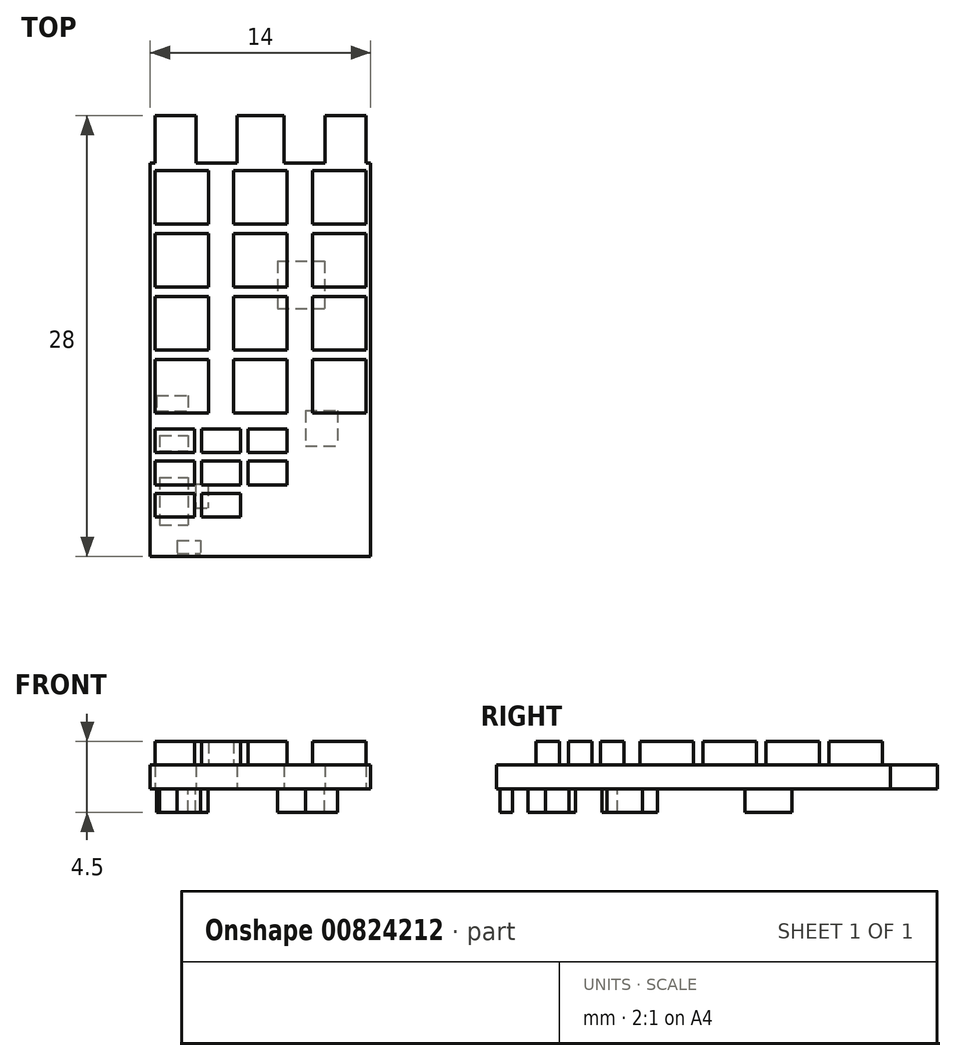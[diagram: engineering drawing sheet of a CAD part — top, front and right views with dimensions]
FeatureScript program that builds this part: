
annotation { "Feature Type Name" : "Feature", "Feature Type Description" : "" }
export const myFeature = defineFeature(function(context is Context, id is Id, definition is map)
    precondition{}
    {
        {
            var Q0;
            Q0=qCreatedBy(makeId("Top.planeOp"),FACE);
            var sketch = newSketch(context, id + "F0", { "sketchPlane" : qUnion([Q0])});
            skLineSegment(sketch, "E0.bottom", {"start": v(7, -14) * mm, "end": v(-7, -14) * mm});
            skLineSegment(sketch, "E0.top", {"start": v(7, 14) * mm, "end": v(-7, 14) * mm});
            skLineSegment(sketch, "E0.left", {"start": v(7, -14) * mm, "end": v(7, 14) * mm});
            skLineSegment(sketch, "E0.right", {"start": v(-7, -14) * mm, "end": v(-7, 14) * mm});
            skPoint(sketch, "E0.middle", {"position": v(0, 0) * mm});
            skLineSegment(sketch, "E1", {"start": v(-4.1, 14) * mm, "end": v(-4.1, 11) * mm});
            skLineSegment(sketch, "E2", {"start": v(-4.1, 11) * mm, "end": v(-1.5, 11) * mm});
            skLineSegment(sketch, "E3", {"start": v(-1.5, 11) * mm, "end": v(-1.5, 14) * mm});
            skLineSegment(sketch, "E4", {"start": v(-1.5, 14) * mm, "end": v(1.5, 14) * mm});
            skLineSegment(sketch, "E5", {"start": v(1.5, 14) * mm, "end": v(1.5, 11) * mm});
            skLineSegment(sketch, "E6", {"start": v(1.5, 11) * mm, "end": v(4.1, 11) * mm});
            skLineSegment(sketch, "E7", {"start": v(4.1, 11) * mm, "end": v(4.1, 14) * mm});
            skLineSegment(sketch, "E8", {"start": v(-6.7, 14) * mm, "end": v(-6.7, 11) * mm});
            skLineSegment(sketch, "E9", {"start": v(-6.7, 11) * mm, "end": v(-7, 11) * mm});
            skLineSegment(sketch, "E10", {"start": v(6.7, 14) * mm, "end": v(6.7, 11) * mm});
            skLineSegment(sketch, "E11", {"start": v(6.7, 11) * mm, "end": v(7, 11) * mm});
            skLineSegment(sketch, "E12", {"start": v(0, 14) * mm, "end": v(0, -14) * mm, "construction": true});
            skSolve(sketch);
        }
        {
            var Q0;
            {var subQ1=sQuery(id+"F0.wireOp",EDGE,"E0.bottom");Q0=makeQuery(id+"F0.imprint","IMPRINT",FACE,{"disambiguationData":[TD([[makeQuery(id+"F0.imprint","IMPRINT",EDGE,{"derivedFrom":subQ1}),-1.0]])]});}
            extrude(context, id + "F1", {"entities" : qUnion([Q0]), "depth" : 1.5 * mm, "offsetDistance" : 25 * mm});
        }
        {
            var Q0;
            Q0=makeQuery(id+"F1.opExtrude","CAP_FACE",FACE,{"disambiguationData":[OSD([sQuery(id+"F0.wireOp",EDGE,"E0.bottom"),sQuery(id+"F0.wireOp",EDGE,"E0.top"),sQuery(id+"F0.wireOp",EDGE,"E0.left"),sQuery(id+"F0.wireOp",EDGE,"E0.right"),sQuery(id+"F0.wireOp",EDGE,"E1"),sQuery(id+"F0.wireOp",EDGE,"E2"),sQuery(id+"F0.wireOp",EDGE,"E3"),sQuery(id+"F0.wireOp",EDGE,"E4"),sQuery(id+"F0.wireOp",EDGE,"E5"),sQuery(id+"F0.wireOp",EDGE,"E6"),sQuery(id+"F0.wireOp",EDGE,"E7"),sQuery(id+"F0.wireOp",EDGE,"E8"),sQuery(id+"F0.wireOp",EDGE,"E9"),sQuery(id+"F0.wireOp",EDGE,"E10"),sQuery(id+"F0.wireOp",EDGE,"E11")])],"isStart":false});
            var sketch = newSketch(context, id + "F2", { "sketchPlane" : qUnion([Q0])});
            skSolve(sketch);
        }
        {
            var Q0;
            Q0=makeQuery(id+"F2.imprint","IMPRINT",FACE,{"disambiguationData":[TD([[makeQuery(id+"F2.imprint","IMPRINT",EDGE,{"derivedFrom":makeQuery(id+"F1.opExtrude","CAP_EDGE",EDGE,{"disambiguationData":[OSD([sQuery(id+"F0.wireOp",EDGE,"E0.bottom")])],"isStart":false})}),-1.0]])]});
            var sketch = newSketch(context, id + "F3", { "sketchPlane" : qUnion([Q0])});
            skLineSegment(sketch, "E13.bottom", {"start": v(-3.3, 10.5) * mm, "end": v(-6.7, 10.5) * mm});
            skLineSegment(sketch, "E13.top", {"start": v(-3.3, 7.1) * mm, "end": v(-6.7, 7.1) * mm});
            skLineSegment(sketch, "E13.left", {"start": v(-3.3, 10.5) * mm, "end": v(-3.3, 7.1) * mm});
            skLineSegment(sketch, "E13.right", {"start": v(-6.7, 10.5) * mm, "end": v(-6.7, 7.1) * mm});
            skPoint(sketch, "E13.middle", {"position": v(-5, 8.8) * mm});
            skLineSegment(sketch, "E14.0.1.0", {"start": v(-6.7, 6.5) * mm, "end": v(-6.7, 3.1) * mm});
            skLineSegment(sketch, "E14.0.1.1", {"start": v(-3.3, 6.5) * mm, "end": v(-6.7, 6.5) * mm});
            skLineSegment(sketch, "E14.0.1.2", {"start": v(-3.3, 6.5) * mm, "end": v(-3.3, 3.1) * mm});
            skLineSegment(sketch, "E14.0.1.3", {"start": v(-3.3, 3.1) * mm, "end": v(-6.7, 3.1) * mm});
            skPoint(sketch, "E14.0.1.4", {"position": v(-5, 4.8) * mm});
            skLineSegment(sketch, "E14.0.2.0", {"start": v(-6.7, 2.5) * mm, "end": v(-6.7, -0.9) * mm});
            skLineSegment(sketch, "E14.0.2.1", {"start": v(-3.3, 2.5) * mm, "end": v(-6.7, 2.5) * mm});
            skLineSegment(sketch, "E14.0.2.2", {"start": v(-3.3, 2.5) * mm, "end": v(-3.3, -0.9) * mm});
            skLineSegment(sketch, "E14.0.2.3", {"start": v(-3.3, -0.9) * mm, "end": v(-6.7, -0.9) * mm});
            skPoint(sketch, "E14.0.2.4", {"position": v(-5, 0.8) * mm});
            skLineSegment(sketch, "E14.0.3.0", {"start": v(-6.7, -1.5) * mm, "end": v(-6.7, -4.9) * mm});
            skLineSegment(sketch, "E14.0.3.1", {"start": v(-3.3, -1.5) * mm, "end": v(-6.7, -1.5) * mm});
            skLineSegment(sketch, "E14.0.3.2", {"start": v(-3.3, -1.5) * mm, "end": v(-3.3, -4.9) * mm});
            skLineSegment(sketch, "E14.0.3.3", {"start": v(-3.3, -4.9) * mm, "end": v(-6.7, -4.9) * mm});
            skPoint(sketch, "E14.0.3.4", {"position": v(-5, -3.2) * mm});
            skLineSegment(sketch, "E14.1.0.0", {"start": v(-1.7, 10.5) * mm, "end": v(-1.7, 7.1) * mm});
            skLineSegment(sketch, "E14.1.0.1", {"start": v(1.7, 10.5) * mm, "end": v(-1.7, 10.5) * mm});
            skLineSegment(sketch, "E14.1.0.2", {"start": v(1.7, 10.5) * mm, "end": v(1.7, 7.1) * mm});
            skLineSegment(sketch, "E14.1.0.3", {"start": v(1.7, 7.1) * mm, "end": v(-1.7, 7.1) * mm});
            skPoint(sketch, "E14.1.0.4", {"position": v(0, 8.8) * mm});
            skLineSegment(sketch, "E14.1.1.0", {"start": v(-1.7, 6.5) * mm, "end": v(-1.7, 3.1) * mm});
            skLineSegment(sketch, "E14.1.1.1", {"start": v(1.7, 6.5) * mm, "end": v(-1.7, 6.5) * mm});
            skLineSegment(sketch, "E14.1.1.2", {"start": v(1.7, 6.5) * mm, "end": v(1.7, 3.1) * mm});
            skLineSegment(sketch, "E14.1.1.3", {"start": v(1.7, 3.1) * mm, "end": v(-1.7, 3.1) * mm});
            skPoint(sketch, "E14.1.1.4", {"position": v(0, 4.8) * mm});
            skLineSegment(sketch, "E14.1.2.0", {"start": v(-1.7, 2.5) * mm, "end": v(-1.7, -0.9) * mm});
            skLineSegment(sketch, "E14.1.2.1", {"start": v(1.7, 2.5) * mm, "end": v(-1.7, 2.5) * mm});
            skLineSegment(sketch, "E14.1.2.2", {"start": v(1.7, 2.5) * mm, "end": v(1.7, -0.9) * mm});
            skLineSegment(sketch, "E14.1.2.3", {"start": v(1.7, -0.9) * mm, "end": v(-1.7, -0.9) * mm});
            skPoint(sketch, "E14.1.2.4", {"position": v(0, 0.8) * mm});
            skLineSegment(sketch, "E14.1.3.0", {"start": v(-1.7, -1.5) * mm, "end": v(-1.7, -4.9) * mm});
            skLineSegment(sketch, "E14.1.3.1", {"start": v(1.7, -1.5) * mm, "end": v(-1.7, -1.5) * mm});
            skLineSegment(sketch, "E14.1.3.2", {"start": v(1.7, -1.5) * mm, "end": v(1.7, -4.9) * mm});
            skLineSegment(sketch, "E14.1.3.3", {"start": v(1.7, -4.9) * mm, "end": v(-1.7, -4.9) * mm});
            skPoint(sketch, "E14.1.3.4", {"position": v(0, -3.2) * mm});
            skLineSegment(sketch, "E14.2.0.0", {"start": v(3.3, 10.5) * mm, "end": v(3.3, 7.1) * mm});
            skLineSegment(sketch, "E14.2.0.1", {"start": v(6.7, 10.5) * mm, "end": v(3.3, 10.5) * mm});
            skLineSegment(sketch, "E14.2.0.2", {"start": v(6.7, 10.5) * mm, "end": v(6.7, 7.1) * mm});
            skLineSegment(sketch, "E14.2.0.3", {"start": v(6.7, 7.1) * mm, "end": v(3.3, 7.1) * mm});
            skPoint(sketch, "E14.2.0.4", {"position": v(5, 8.8) * mm});
            skLineSegment(sketch, "E14.2.1.0", {"start": v(3.3, 6.5) * mm, "end": v(3.3, 3.1) * mm});
            skLineSegment(sketch, "E14.2.1.1", {"start": v(6.7, 6.5) * mm, "end": v(3.3, 6.5) * mm});
            skLineSegment(sketch, "E14.2.1.2", {"start": v(6.7, 6.5) * mm, "end": v(6.7, 3.1) * mm});
            skLineSegment(sketch, "E14.2.1.3", {"start": v(6.7, 3.1) * mm, "end": v(3.3, 3.1) * mm});
            skPoint(sketch, "E14.2.1.4", {"position": v(5, 4.8) * mm});
            skLineSegment(sketch, "E14.2.2.0", {"start": v(3.3, 2.5) * mm, "end": v(3.3, -0.9) * mm});
            skLineSegment(sketch, "E14.2.2.1", {"start": v(6.7, 2.5) * mm, "end": v(3.3, 2.5) * mm});
            skLineSegment(sketch, "E14.2.2.2", {"start": v(6.7, 2.5) * mm, "end": v(6.7, -0.9) * mm});
            skLineSegment(sketch, "E14.2.2.3", {"start": v(6.7, -0.9) * mm, "end": v(3.3, -0.9) * mm});
            skPoint(sketch, "E14.2.2.4", {"position": v(5, 0.8) * mm});
            skLineSegment(sketch, "E14.2.3.0", {"start": v(3.3, -1.5) * mm, "end": v(3.3, -4.9) * mm});
            skLineSegment(sketch, "E14.2.3.1", {"start": v(6.7, -1.5) * mm, "end": v(3.3, -1.5) * mm});
            skLineSegment(sketch, "E14.2.3.2", {"start": v(6.7, -1.5) * mm, "end": v(6.7, -4.9) * mm});
            skLineSegment(sketch, "E14.2.3.3", {"start": v(6.7, -4.9) * mm, "end": v(3.3, -4.9) * mm});
            skPoint(sketch, "E14.2.3.4", {"position": v(5, -3.2) * mm});
            skLineSegment(sketch, "E14.direction1", {"start": v(-6.7, 7.1) * mm, "end": v(-1.7, 7.1) * mm, "construction": true});
            skLineSegment(sketch, "E14.direction2", {"start": v(-6.7, 7.1) * mm, "end": v(-6.7, 3.1) * mm, "construction": true});
            skLineSegment(sketch, "E15.bottom", {"start": v(-4.2, -7.4) * mm, "end": v(-6.7, -7.4) * mm});
            skLineSegment(sketch, "E15.top", {"start": v(-4.2, -5.9) * mm, "end": v(-6.7, -5.9) * mm});
            skLineSegment(sketch, "E15.left", {"start": v(-4.2, -7.4) * mm, "end": v(-4.2, -5.9) * mm});
            skLineSegment(sketch, "E15.right", {"start": v(-6.7, -7.4) * mm, "end": v(-6.7, -5.9) * mm});
            skPoint(sketch, "E15.middle", {"position": v(-5.45, -6.65) * mm});
            skLineSegment(sketch, "E16.0.1.0", {"start": v(-6.7, -9.45) * mm, "end": v(-6.7, -7.95) * mm});
            skLineSegment(sketch, "E16.0.1.1", {"start": v(-4.2, -7.95) * mm, "end": v(-6.7, -7.95) * mm});
            skLineSegment(sketch, "E16.0.1.2", {"start": v(-4.2, -9.45) * mm, "end": v(-6.7, -9.45) * mm});
            skPoint(sketch, "E16.0.1.3", {"position": v(-5.45, -8.7) * mm});
            skLineSegment(sketch, "E16.0.1.4", {"start": v(-4.2, -9.45) * mm, "end": v(-4.2, -7.95) * mm});
            skLineSegment(sketch, "E16.1.0.0", {"start": v(-3.75, -7.4) * mm, "end": v(-3.75, -5.9) * mm});
            skLineSegment(sketch, "E16.1.0.1", {"start": v(-1.25, -5.9) * mm, "end": v(-3.75, -5.9) * mm});
            skLineSegment(sketch, "E16.1.0.2", {"start": v(-1.25, -7.4) * mm, "end": v(-3.75, -7.4) * mm});
            skPoint(sketch, "E16.1.0.3", {"position": v(-2.5, -6.65) * mm});
            skLineSegment(sketch, "E16.1.0.4", {"start": v(-1.25, -7.4) * mm, "end": v(-1.25, -5.9) * mm});
            skLineSegment(sketch, "E16.1.1.0", {"start": v(-3.75, -9.45) * mm, "end": v(-3.75, -7.95) * mm});
            skLineSegment(sketch, "E16.1.1.1", {"start": v(-1.25, -7.95) * mm, "end": v(-3.75, -7.95) * mm});
            skLineSegment(sketch, "E16.1.1.2", {"start": v(-1.25, -9.45) * mm, "end": v(-3.75, -9.45) * mm});
            skPoint(sketch, "E16.1.1.3", {"position": v(-2.5, -8.7) * mm});
            skLineSegment(sketch, "E16.1.1.4", {"start": v(-1.25, -9.45) * mm, "end": v(-1.25, -7.95) * mm});
            skLineSegment(sketch, "E16.2.0.0", {"start": v(-0.8, -7.4) * mm, "end": v(-0.8, -5.9) * mm});
            skLineSegment(sketch, "E16.2.0.1", {"start": v(1.7, -5.9) * mm, "end": v(-0.8, -5.9) * mm});
            skLineSegment(sketch, "E16.2.0.2", {"start": v(1.7, -7.4) * mm, "end": v(-0.8, -7.4) * mm});
            skPoint(sketch, "E16.2.0.3", {"position": v(0.45, -6.65) * mm});
            skLineSegment(sketch, "E16.2.0.4", {"start": v(1.7, -7.4) * mm, "end": v(1.7, -5.9) * mm});
            skLineSegment(sketch, "E16.2.1.0", {"start": v(-0.8, -9.45) * mm, "end": v(-0.8, -7.95) * mm});
            skLineSegment(sketch, "E16.2.1.1", {"start": v(1.7, -7.95) * mm, "end": v(-0.8, -7.95) * mm});
            skLineSegment(sketch, "E16.2.1.2", {"start": v(1.7, -9.45) * mm, "end": v(-0.8, -9.45) * mm});
            skPoint(sketch, "E16.2.1.3", {"position": v(0.45, -8.7) * mm});
            skLineSegment(sketch, "E16.2.1.4", {"start": v(1.7, -9.45) * mm, "end": v(1.7, -7.95) * mm});
            skLineSegment(sketch, "E16.direction1", {"start": v(-6.7, -7.4) * mm, "end": v(-3.75, -7.4) * mm, "construction": true});
            skLineSegment(sketch, "E16.direction2", {"start": v(-6.7, -7.4) * mm, "end": v(-6.7, -9.45) * mm, "construction": true});
            skLineSegment(sketch, "E17.0.0.2", {"start": v(-6.7, -11.5) * mm, "end": v(-6.7, -10) * mm});
            skLineSegment(sketch, "E17.3.0.2", {"start": v(-4.2, -10) * mm, "end": v(-6.7, -10) * mm});
            skLineSegment(sketch, "E17.6.0.2", {"start": v(-4.2, -11.5) * mm, "end": v(-6.7, -11.5) * mm});
            skPoint(sketch, "E17.9.0.2", {"position": v(-5.45, -10.75) * mm});
            skLineSegment(sketch, "E17.10.0.2", {"start": v(-4.2, -11.5) * mm, "end": v(-4.2, -10) * mm});
            skLineSegment(sketch, "E17.0.1.2", {"start": v(-3.75, -11.5) * mm, "end": v(-3.75, -10) * mm});
            skLineSegment(sketch, "E17.3.1.2", {"start": v(-1.25, -10) * mm, "end": v(-3.75, -10) * mm});
            skLineSegment(sketch, "E17.6.1.2", {"start": v(-1.25, -11.5) * mm, "end": v(-3.75, -11.5) * mm});
            skPoint(sketch, "E17.9.1.2", {"position": v(-2.5, -10.75) * mm});
            skLineSegment(sketch, "E17.10.1.2", {"start": v(-1.25, -11.5) * mm, "end": v(-1.25, -10) * mm});
            skLineSegment(sketch, "E17.0.2.2", {"start": v(-0.8, -11.5) * mm, "end": v(-0.8, -10) * mm, "construction": true});
            skLineSegment(sketch, "E17.3.2.2", {"start": v(1.7, -10) * mm, "end": v(-0.8, -10) * mm, "construction": true});
            skLineSegment(sketch, "E17.6.2.2", {"start": v(1.7, -11.5) * mm, "end": v(-0.8, -11.5) * mm, "construction": true});
            skPoint(sketch, "E17.9.2.2", {"position": v(0.45, -10.75) * mm});
            skLineSegment(sketch, "E17.10.2.2", {"start": v(1.7, -11.5) * mm, "end": v(1.7, -10) * mm, "construction": true});
            skSolve(sketch);
        }
        {
            var Q0;
            Q0 = qSketchRegion(id + "F3", true);
            extrude(context, id + "F4", {"entities" : qUnion([Q0]), "operationType" : NewBodyOperationType.ADD, "depth" : 1.5 * mm, "offsetDistance" : 25 * mm});
        }
        {
            var Q0;
            Q0=makeQuery(id+"F1.opExtrude","CAP_FACE",FACE,{"disambiguationData":[OSD([sQuery(id+"F0.wireOp",EDGE,"E0.bottom"),sQuery(id+"F0.wireOp",EDGE,"E0.top"),sQuery(id+"F0.wireOp",EDGE,"E0.left"),sQuery(id+"F0.wireOp",EDGE,"E0.right"),sQuery(id+"F0.wireOp",EDGE,"E1"),sQuery(id+"F0.wireOp",EDGE,"E2"),sQuery(id+"F0.wireOp",EDGE,"E3"),sQuery(id+"F0.wireOp",EDGE,"E4"),sQuery(id+"F0.wireOp",EDGE,"E5"),sQuery(id+"F0.wireOp",EDGE,"E6"),sQuery(id+"F0.wireOp",EDGE,"E7"),sQuery(id+"F0.wireOp",EDGE,"E8"),sQuery(id+"F0.wireOp",EDGE,"E9"),sQuery(id+"F0.wireOp",EDGE,"E10"),sQuery(id+"F0.wireOp",EDGE,"E11")])],"isStart":true});
            var sketch = newSketch(context, id + "F5", { "sketchPlane" : qUnion([Q0])});
            skLineSegment(sketch, "E18.bottom", {"start": v(1.07, -4.76) * mm, "end": v(4.07, -4.76) * mm});
            skLineSegment(sketch, "E18.top", {"start": v(1.07, -1.76) * mm, "end": v(4.07, -1.76) * mm});
            skLineSegment(sketch, "E18.left", {"start": v(1.07, -4.76) * mm, "end": v(1.07, -1.76) * mm});
            skLineSegment(sketch, "E18.right", {"start": v(4.07, -4.76) * mm, "end": v(4.07, -1.76) * mm});
            skPoint(sketch, "E18.middle", {"position": v(2.57, -3.26) * mm});
            skLineSegment(sketch, "E19.bottom", {"start": v(2.85, 4.74) * mm, "end": v(4.9, 4.74) * mm});
            skLineSegment(sketch, "E19.top", {"start": v(2.85, 6.99) * mm, "end": v(4.9, 6.99) * mm});
            skLineSegment(sketch, "E19.left", {"start": v(2.85, 4.74) * mm, "end": v(2.85, 6.99) * mm});
            skLineSegment(sketch, "E19.right", {"start": v(4.9, 4.74) * mm, "end": v(4.9, 6.99) * mm});
            skPoint(sketch, "E19.middle", {"position": v(3.87, 5.86) * mm});
            skLineSegment(sketch, "E20.bottom", {"start": v(-6.4, 9) * mm, "end": v(-4.6, 9) * mm});
            skLineSegment(sketch, "E20.top", {"start": v(-6.4, 12) * mm, "end": v(-4.6, 12) * mm});
            skLineSegment(sketch, "E20.left", {"start": v(-6.4, 9) * mm, "end": v(-6.4, 12) * mm});
            skLineSegment(sketch, "E20.right", {"start": v(-4.6, 9) * mm, "end": v(-4.6, 12) * mm});
            skPoint(sketch, "E20.middle", {"position": v(-5.5, 10.5) * mm});
            skLineSegment(sketch, "E21.bottom", {"start": v(-6.4, 6.31) * mm, "end": v(-4.6, 6.31) * mm});
            skLineSegment(sketch, "E21.top", {"start": v(-6.4, 7.31) * mm, "end": v(-4.6, 7.31) * mm});
            skLineSegment(sketch, "E21.left", {"start": v(-6.4, 6.31) * mm, "end": v(-6.4, 7.31) * mm});
            skLineSegment(sketch, "E21.right", {"start": v(-4.6, 6.31) * mm, "end": v(-4.6, 7.31) * mm});
            skPoint(sketch, "E21.middle", {"position": v(-5.5, 6.81) * mm});
            skLineSegment(sketch, "E22.bottom", {"start": v(-6.6, 3.78) * mm, "end": v(-4.6, 3.78) * mm});
            skLineSegment(sketch, "E22.top", {"start": v(-6.6, 4.78) * mm, "end": v(-4.6, 4.78) * mm});
            skLineSegment(sketch, "E22.left", {"start": v(-6.6, 3.78) * mm, "end": v(-6.6, 4.78) * mm});
            skLineSegment(sketch, "E22.right", {"start": v(-4.6, 3.78) * mm, "end": v(-4.6, 4.78) * mm});
            skPoint(sketch, "E22.middle", {"position": v(-5.6, 4.28) * mm});
            skLineSegment(sketch, "E23.bottom", {"start": v(-4.13, 9.4) * mm, "end": v(-3.33, 9.4) * mm});
            skLineSegment(sketch, "E23.top", {"start": v(-4.13, 10.9) * mm, "end": v(-3.33, 10.9) * mm});
            skLineSegment(sketch, "E23.left", {"start": v(-4.13, 9.4) * mm, "end": v(-4.13, 10.9) * mm});
            skLineSegment(sketch, "E23.right", {"start": v(-3.33, 9.4) * mm, "end": v(-3.33, 10.9) * mm});
            skPoint(sketch, "E23.middle", {"position": v(-3.73, 10.16) * mm});
            skLineSegment(sketch, "E24.bottom", {"start": v(-5.3, 13) * mm, "end": v(-3.8, 13) * mm});
            skLineSegment(sketch, "E24.top", {"start": v(-5.3, 13.8) * mm, "end": v(-3.8, 13.8) * mm});
            skLineSegment(sketch, "E24.left", {"start": v(-5.3, 13) * mm, "end": v(-5.3, 13.8) * mm});
            skLineSegment(sketch, "E24.right", {"start": v(-3.8, 13) * mm, "end": v(-3.8, 13.8) * mm});
            skPoint(sketch, "E24.middle", {"position": v(-4.54, 13.4) * mm});
            skSolve(sketch);
        }
        {
            var Q0;
            Q0 = qSketchRegion(id + "F5", true);
            extrude(context, id + "F6", {"entities" : qUnion([Q0]), "operationType" : NewBodyOperationType.ADD, "depth" : 1.5 * mm, "offsetDistance" : 25 * mm});
        }
    });
